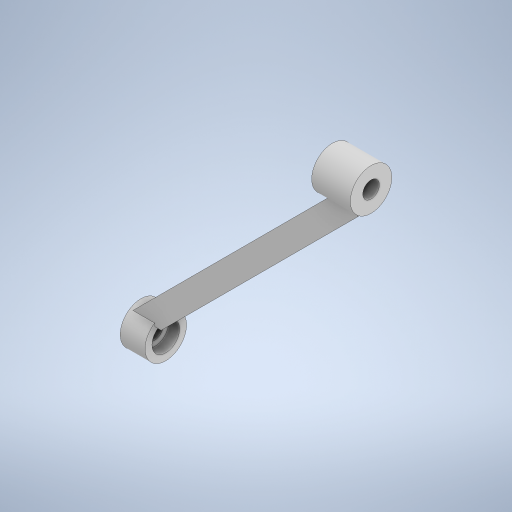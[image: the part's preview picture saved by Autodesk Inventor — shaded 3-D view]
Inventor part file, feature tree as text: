
AUTODESK INVENTOR PART (.ipt)
format: ipt  version: 2023 (Build 270158000, 158)  size: 294,400 bytes
history: native  units: mm
features: extrude x5, sketch x4, projected_geometry x2, plane x1
ambient origin geometry x8: Origin, YZ Plane, XZ Plane, XY Plane, X Axis, Y Axis, Z Axis, Center Point
bodies: Solid1 (feature_tree)
feature tree (12):
  sketch  "Sketch1"  dims[d0=6.0mm d1=15.0mm]
  extrude  "Extrusion1"  Depth=15.0mm
  extrude  "Extrusion2"  Depth=14.0mm
  extrude  "Extrusion3"  Depth=4.0mm
  plane  "Work Plane1"
  extrude  "Extrusion4"  Depth=8.0mm TaperAngle=0.0deg
  extrude  "Extrusion5"  Depth=4.0mm
  sketch  "Sketch2"  dims[d2=14.0mm d3=0.0mm d4=100.0mm]
  projected_geometry  "Projected Loop1"
  sketch  "Sketch3"  dims[d5=45.0deg d6=4.0mm]
  projected_geometry  "Projected Loop2"
  sketch  "Sketch4"  dims[d7=4.0mm d8=8.0mm d9=0.0mm d10=8.871019mm d12=60.0mm d13=2.0mm d14=0.0mm d15=15.0mm d16=6.0mm d17=5.240974mm d18=9.0mm d19=0.0mm d20=10.0mm d21=9.0mm d22=4.0mm d23=0.0mm d24=0.0mm]
